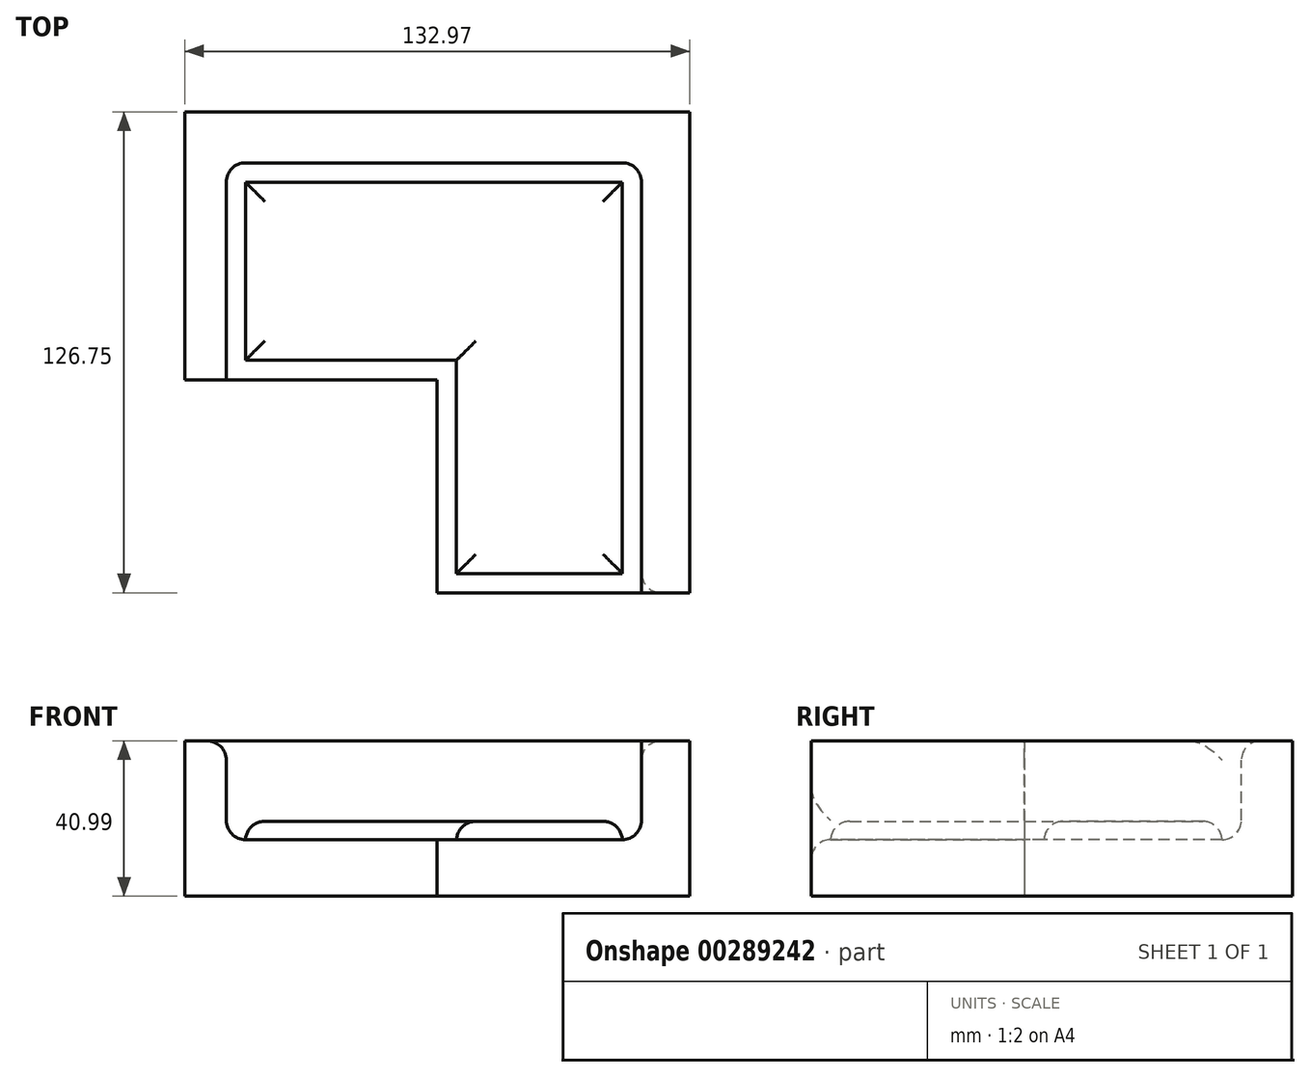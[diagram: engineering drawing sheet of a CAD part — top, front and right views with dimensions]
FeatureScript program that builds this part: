
annotation { "Feature Type Name" : "Feature", "Feature Type Description" : "" }
export const myFeature = defineFeature(function(context is Context, id is Id, definition is map)
    precondition{}
    {
        {
            var Q0;
            Q0=qCreatedBy(makeId("Front.planeOp"),FACE);
            var sketch = newSketch(context, id + "F0", { "sketchPlane" : qUnion([Q0])});
            skLineSegment(sketch, "E0.bottom", {"start": v(-65.6, 14.69) * mm, "end": v(67.37, 14.69) * mm});
            skLineSegment(sketch, "E0.top", {"start": v(-65.6, -26.3) * mm, "end": v(67.37, -26.3) * mm});
            skLineSegment(sketch, "E0.left", {"start": v(-65.6, 14.69) * mm, "end": v(-65.6, -26.3) * mm});
            skLineSegment(sketch, "E0.right", {"start": v(67.37, 14.69) * mm, "end": v(67.37, -26.3) * mm});
            skSolve(sketch);
        }
        {
            var Q0;
            Q0 = qSketchRegion(id + "F0", true);
            extrude(context, id + "F1", {"entities" : qUnion([Q0]), "endBound" : BoundingType.SYMMETRIC, "depth" : 70.61 * mm});
        }
        {
            var Q0;
            Q0=makeQuery(id+"F1.opExtrude","CAP_FACE",FACE,{"disambiguationData":[OSD([sQuery(id+"F0.wireOp",EDGE,"E0.bottom"),sQuery(id+"F0.wireOp",EDGE,"E0.top"),sQuery(id+"F0.wireOp",EDGE,"E0.left"),sQuery(id+"F0.wireOp",EDGE,"E0.right")])],"isStart":false});
            var sketch = newSketch(context, id + "F2", { "sketchPlane" : qUnion([Q0])});
            skLineSegment(sketch, "E1.bottom", {"start": v(54.7, -11.37) * mm, "end": v(-54.7, -11.37) * mm});
            skLineSegment(sketch, "E1.top", {"start": v(54.7, 40.74) * mm, "end": v(-54.7, 40.74) * mm});
            skLineSegment(sketch, "E1.left", {"start": v(54.7, -11.37) * mm, "end": v(54.7, 40.74) * mm});
            skLineSegment(sketch, "E1.right", {"start": v(-54.7, -11.37) * mm, "end": v(-54.7, 40.74) * mm});
            skPoint(sketch, "E1.middle", {"position": v(0, 14.69) * mm});
            skPoint(sketch, "E1.middle.positionSnap0", {"position": v(0.89, 14.69) * mm});
            skPoint(sketch, "E1.centerSnap0", {"position": v(0.89, 14.69) * mm});
            skSolve(sketch);
        }
        {
            var Q0;
            Q0 = qSketchRegion(id + "F2", true);
            extrude(context, id + "F3", {"entities" : qUnion([Q0]), "operationType" : NewBodyOperationType.REMOVE, "oppositeDirection" : true, "depth" : 57.15 * mm});
        }
        {
            var Q0;
            Q0=makeQuery(id+"F1.opExtrude","CAP_FACE",FACE,{"disambiguationData":[OSD([sQuery(id+"F0.wireOp",EDGE,"E0.bottom"),sQuery(id+"F0.wireOp",EDGE,"E0.top"),sQuery(id+"F0.wireOp",EDGE,"E0.left"),sQuery(id+"F0.wireOp",EDGE,"E0.right")])],"isStart":false});
            var sketch = newSketch(context, id + "F4", { "sketchPlane" : qUnion([Q0])});
            skLineSegment(sketch, "E2.bottom", {"start": v(67.37, 14.69) * mm, "end": v(0.89, 14.69) * mm});
            skLineSegment(sketch, "E2.top", {"start": v(67.37, -26.3) * mm, "end": v(0.89, -26.3) * mm});
            skLineSegment(sketch, "E2.left", {"start": v(67.37, 14.69) * mm, "end": v(67.37, -26.3) * mm});
            skLineSegment(sketch, "E2.right", {"start": v(0.89, 14.69) * mm, "end": v(0.89, -26.3) * mm});
            skSolve(sketch);
        }
        {
            var Q0;
            Q0 = qSketchRegion(id + "F4", true);
            extrude(context, id + "F5", {"entities" : qUnion([Q0]), "operationType" : NewBodyOperationType.ADD, "depth" : 56.13 * mm});
        }
        {
            var Q0;
            Q0=makeQuery(id+"F5.opExtrude","CAP_FACE",FACE,{"disambiguationData":[OSD([sQuery(id+"F4.wireOp",EDGE,"E2.bottom"),sQuery(id+"F4.wireOp",EDGE,"E2.top"),sQuery(id+"F4.wireOp",EDGE,"E2.left"),sQuery(id+"F4.wireOp",EDGE,"E2.right")])],"isStart":true});
            var sketch = newSketch(context, id + "F6", { "sketchPlane" : qUnion([Q0])});
            skLineSegment(sketch, "E3.bottom", {"start": v(-54.7, 14.69) * mm, "end": v(-0.89, 14.69) * mm});
            skLineSegment(sketch, "E3.top", {"start": v(-54.7, -11.37) * mm, "end": v(-0.89, -11.37) * mm});
            skLineSegment(sketch, "E3.left", {"start": v(-54.7, 14.69) * mm, "end": v(-54.7, -11.37) * mm});
            skLineSegment(sketch, "E3.right", {"start": v(-0.89, 14.69) * mm, "end": v(-0.89, -11.37) * mm});
            skSolve(sketch);
        }
        {
            var Q0;
            Q0 = qSketchRegion(id + "F6", true);
            extrude(context, id + "F7", {"entities" : qUnion([Q0]), "operationType" : NewBodyOperationType.REMOVE, "oppositeDirection" : true, "depth" : 59.69 * mm});
        }
        {
            var Q0;
            Q0=makeQuery(id+"F3.boolean.opBoolean","COPY",EDGE,{"derivedFrom":makeQuery(id+"F3.opExtrude","SWEPT_EDGE",EDGE,{"disambiguationData":[OSD([sQuery(id+"F2.wireOp",EDGE,"E1.bottom"),sQuery(id+"F2.wireOp",EDGE,"E1.right")])]})});
            var Q1;
            Q1=makeQuery(id+"F3.boolean.opBoolean","INTERSECT",EDGE,{"derivedFrom":[makeQuery(id+"F1.opExtrude","SWEPT_FACE",FACE,{"disambiguationData":[OSD([sQuery(id+"F0.wireOp",EDGE,"E0.bottom")])]}),makeQuery(id+"F3.opExtrude","SWEPT_FACE",FACE,{"disambiguationData":[OSD([sQuery(id+"F2.wireOp",EDGE,"E1.right")])]})]});
            var Q2;
            Q2=makeQuery(id+"F3.boolean.opBoolean","COPY",EDGE,{"derivedFrom":makeQuery(id+"F3.opExtrude","CAP_EDGE",EDGE,{"disambiguationData":[OSD([sQuery(id+"F2.wireOp",EDGE,"E1.right")])],"isStart":false})});
            var Q3;
            Q3=makeQuery(id+"F3.boolean.opBoolean","INTERSECT",EDGE,{"derivedFrom":[makeQuery(id+"F1.opExtrude","SWEPT_FACE",FACE,{"disambiguationData":[OSD([sQuery(id+"F0.wireOp",EDGE,"E0.bottom")])]}),makeQuery(id+"F3.opExtrude","CAP_FACE",FACE,{"disambiguationData":[OSD([sQuery(id+"F2.wireOp",EDGE,"E1.bottom"),sQuery(id+"F2.wireOp",EDGE,"E1.top"),sQuery(id+"F2.wireOp",EDGE,"E1.left"),sQuery(id+"F2.wireOp",EDGE,"E1.right")])],"isStart":false})]});
            var Q4;
            Q4=makeQuery(id+"F3.boolean.opBoolean","COPY",EDGE,{"derivedFrom":makeQuery(id+"F3.opExtrude","CAP_EDGE",EDGE,{"disambiguationData":[OSD([sQuery(id+"F2.wireOp",EDGE,"E1.bottom")])],"isStart":false})});
            var Q5;
            Q5=makeQuery(id+"F7.boolean.opBoolean","MERGE",EDGE,{"derivedFrom":[makeQuery(id+"F3.boolean.opBoolean","COPY",EDGE,{"derivedFrom":makeQuery(id+"F3.opExtrude","SWEPT_EDGE",EDGE,{"disambiguationData":[OSD([sQuery(id+"F2.wireOp",EDGE,"E1.bottom"),sQuery(id+"F2.wireOp",EDGE,"E1.left")])]})}),makeQuery(id+"F7.opExtrude","SWEPT_EDGE",EDGE,{"disambiguationData":[OSD([sQuery(id+"F6.wireOp",EDGE,"E3.top"),sQuery(id+"F6.wireOp",EDGE,"E3.left")])]})]});
            var Q6;
            Q6=makeQuery(id+"F3.boolean.opBoolean","COPY",EDGE,{"derivedFrom":makeQuery(id+"F3.opExtrude","CAP_EDGE",EDGE,{"disambiguationData":[OSD([sQuery(id+"F2.wireOp",EDGE,"E1.left")])],"isStart":false})});
            var Q7;
            Q7=makeQuery(id+"F7.boolean.opBoolean","MERGE",EDGE,{"derivedFrom":[makeQuery(id+"F3.boolean.opBoolean","INTERSECT",EDGE,{"derivedFrom":[makeQuery(id+"F1.opExtrude","SWEPT_FACE",FACE,{"disambiguationData":[OSD([sQuery(id+"F0.wireOp",EDGE,"E0.bottom")])]}),makeQuery(id+"F3.opExtrude","SWEPT_FACE",FACE,{"disambiguationData":[OSD([sQuery(id+"F2.wireOp",EDGE,"E1.left")])]})]}),makeQuery(id+"F7.opExtrude","SWEPT_EDGE",EDGE,{"disambiguationData":[OSD([sQuery(id+"F6.wireOp",EDGE,"E3.bottom"),sQuery(id+"F6.wireOp",EDGE,"E3.left")])]})]});
            var Q8;
            {var subQ0=sQuery(id+"F2.wireOp",EDGE,"E1.bottom");Q8=makeQuery(id+"F5.boolean.opBoolean","SPLIT",EDGE,{"disambiguationData":[topologyDisambiguationEdgeConnected([makeQuery(id+"F1.opExtrude","CAP_FACE",FACE,{"disambiguationData":[OSD([sQuery(id+"F0.wireOp",EDGE,"E0.bottom"),sQuery(id+"F0.wireOp",EDGE,"E0.top"),sQuery(id+"F0.wireOp",EDGE,"E0.left"),sQuery(id+"F0.wireOp",EDGE,"E0.right")])],"isStart":false})])],"derivedFrom":makeQuery(id+"F3.boolean.opBoolean","COPY",EDGE,{"derivedFrom":makeQuery(id+"F3.opExtrude","CAP_EDGE",EDGE,{"disambiguationData":[OSD([subQ0])],"isStart":true})})});}
            var Q9;
            Q9=makeQuery(id+"F7.boolean.opBoolean","COPY",EDGE,{"derivedFrom":makeQuery(id+"F7.opExtrude","SWEPT_EDGE",EDGE,{"disambiguationData":[OSD([sQuery(id+"F6.wireOp",EDGE,"E3.top"),sQuery(id+"F6.wireOp",EDGE,"E3.right")])]})});
            var Q10;
            Q10=makeQuery(id+"F7.boolean.opBoolean","INTERSECT",EDGE,{"derivedFrom":[makeQuery(id+"F5.opExtrude","CAP_FACE",FACE,{"disambiguationData":[OSD([sQuery(id+"F4.wireOp",EDGE,"E2.bottom"),sQuery(id+"F4.wireOp",EDGE,"E2.top"),sQuery(id+"F4.wireOp",EDGE,"E2.left"),sQuery(id+"F4.wireOp",EDGE,"E2.right")])],"isStart":false}),makeQuery(id+"F7.opExtrude","SWEPT_FACE",FACE,{"disambiguationData":[OSD([sQuery(id+"F6.wireOp",EDGE,"E3.top")])]})]});
            fillet(context, id + "F8", {"entities" : qUnion([Q0, Q1, Q2, Q3, Q4, Q5, Q6, Q7, Q8, Q9, Q10]), "radius" : 5.08 * mm, "tangentPropagation" : true, "allowEdgeOverflow" : false});
        }
        {
            var Q0;
            Q0=makeQuery(id+"F7.boolean.opBoolean","MERGE",FACE,{"derivedFrom":[makeQuery(id+"F3.boolean.opBoolean","COPY",FACE,{"derivedFrom":makeQuery(id+"F3.opExtrude","SWEPT_FACE",FACE,{"disambiguationData":[OSD([sQuery(id+"F2.wireOp",EDGE,"E1.bottom")])]})}),makeQuery(id+"F7.opExtrude","SWEPT_FACE",FACE,{"disambiguationData":[OSD([sQuery(id+"F6.wireOp",EDGE,"E3.top")])]})]});
            var sketch = newSketch(context, id + "F9", { "sketchPlane" : qUnion([Q0])});
            skLineSegment(sketch, "E4.bottom", {"start": v(-49.62, 16.76) * mm, "end": v(49.62, 16.76) * mm});
            skLineSegment(sketch, "E4.top", {"start": v(-49.62, -30.15) * mm, "end": v(49.62, -30.15) * mm});
            skLineSegment(sketch, "E4.left", {"start": v(-49.62, 16.76) * mm, "end": v(-49.62, -30.15) * mm});
            skLineSegment(sketch, "E4.right", {"start": v(49.62, 16.76) * mm, "end": v(49.62, -30.15) * mm});
            skSolve(sketch);
        }
        {
            var Q0;
            Q0 = qSketchRegion(id + "F9", true);
            extrude(context, id + "F10", {"entities" : qUnion([Q0]), "operationType" : NewBodyOperationType.ADD, "depth" : 4.83 * mm});
        }
        {
            var Q0;
            Q0=makeQuery(id+"F7.boolean.opBoolean","MERGE",FACE,{"derivedFrom":[makeQuery(id+"F3.boolean.opBoolean","COPY",FACE,{"derivedFrom":makeQuery(id+"F3.opExtrude","SWEPT_FACE",FACE,{"disambiguationData":[OSD([sQuery(id+"F2.wireOp",EDGE,"E1.bottom")])]})}),makeQuery(id+"F7.opExtrude","SWEPT_FACE",FACE,{"disambiguationData":[OSD([sQuery(id+"F6.wireOp",EDGE,"E3.top")])]})]});
            var sketch = newSketch(context, id + "F11", { "sketchPlane" : qUnion([Q0])});
            skLineSegment(sketch, "E5.bottom", {"start": v(49.62, -30.15) * mm, "end": v(5.97, -30.15) * mm});
            skLineSegment(sketch, "E5.top", {"start": v(49.62, -86.36) * mm, "end": v(5.97, -86.36) * mm});
            skLineSegment(sketch, "E5.left", {"start": v(49.62, -30.15) * mm, "end": v(49.62, -86.36) * mm});
            skLineSegment(sketch, "E5.right", {"start": v(5.97, -30.15) * mm, "end": v(5.97, -86.36) * mm});
            skSolve(sketch);
        }
        {
            var Q0;
            Q0 = qSketchRegion(id + "F11", true);
            extrude(context, id + "F12", {"entities" : qUnion([Q0]), "operationType" : NewBodyOperationType.ADD, "depth" : 4.83 * mm});
        }
        {
            var Q0;
            Q0=makeQuery(id+"F12.opExtrude","CAP_EDGE",EDGE,{"disambiguationData":[OSD([sQuery(id+"F11.wireOp",EDGE,"E5.top")])],"isStart":false});
            var Q1;
            Q1=makeQuery(id+"F12.opExtrude","CAP_EDGE",EDGE,{"disambiguationData":[OSD([sQuery(id+"F11.wireOp",EDGE,"E5.right")])],"isStart":false});
            var Q2;
            Q2=makeQuery(id+"F10.opExtrude","CAP_EDGE",EDGE,{"disambiguationData":[OSD([sQuery(id+"F9.wireOp",EDGE,"E4.top")])],"isStart":false});
            var Q3;
            Q3=makeQuery(id+"F12.boolean.opBoolean","MERGE",EDGE,{"derivedFrom":[makeQuery(id+"F10.opExtrude","CAP_EDGE",EDGE,{"disambiguationData":[OSD([sQuery(id+"F9.wireOp",EDGE,"E4.right")])],"isStart":false}),makeQuery(id+"F12.opExtrude","CAP_EDGE",EDGE,{"disambiguationData":[OSD([sQuery(id+"F11.wireOp",EDGE,"E5.left")])],"isStart":false})]});
            var Q4;
            Q4=makeQuery(id+"F10.opExtrude","CAP_EDGE",EDGE,{"disambiguationData":[OSD([sQuery(id+"F9.wireOp",EDGE,"E4.bottom")])],"isStart":false});
            var Q5;
            Q5=makeQuery(id+"F10.opExtrude","CAP_EDGE",EDGE,{"disambiguationData":[OSD([sQuery(id+"F9.wireOp",EDGE,"E4.left")])],"isStart":false});
            fillet(context, id + "F13", {"entities" : qUnion([Q0, Q1, Q2, Q3, Q4, Q5]), "radius" : 5.08 * mm, "tangentPropagation" : true, "allowEdgeOverflow" : false});
        }
    });
